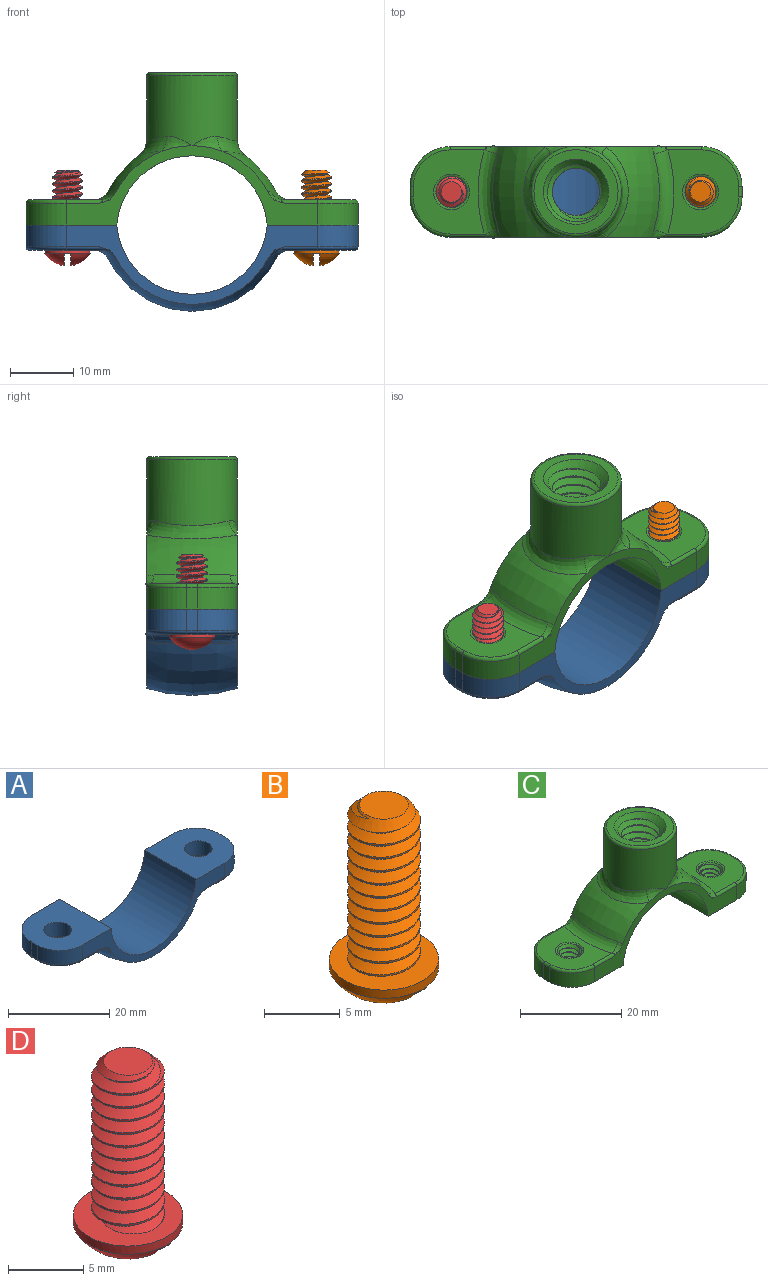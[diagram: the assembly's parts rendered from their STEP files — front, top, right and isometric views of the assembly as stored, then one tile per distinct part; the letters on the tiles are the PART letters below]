
ASSEMBLY  parts=4 mates=3
PART A: 34 faces, bbox 54.3x18.3x14.5 mm
  f0: revolved ~26.09x14.29mm, area 452.7mm2, adj f3,f4,f28,f29,f30,f31,f32,f33
  f1: plane 14.33x14.29mm, normal (0,0,1), area 164.3mm2, adj f3,f4,f5,f8,f10,f11,f14
  f2: plane 14.33x14.29mm, normal (0,0,1), area 164.3mm2, adj f3,f4,f5,f6,f12,f13,f15
  f3: plane 40.53x13.36mm, normal (0,-1,0), area 108.2mm2, adj f0,f1,f2,f5,f10,f13,f16,f21
  f4: plane 40.53x13.36mm, normal (0,1,0), area 108.2mm2, adj f0,f1,f2,f5,f11,f12,f20,f25
  f5: cylinder r=11.91mm len=23.73mm, axis (0,1,0), area 506.1mm2, adj f1,f2,f3,f4
  f6: plane 3.45x1.59mm, normal (-1,0,0), area 5.5mm2, adj f2,f12,f13,f18
  f7: plane 13.28x11.21mm, normal (0,0,-1), area 92.8mm2, adj f16,f17,f18,f19,f20,f26,f32
  f8: plane 3.45x1.59mm, normal (1,0,0), area 5.5mm2, adj f1,f10,f11,f23
  f9: plane 13.28x11.21mm, normal (0,0,-1), area 92.8mm2, adj f21,f22,f23,f24,f25,f27,f29
  f10: cylinder r=6.35mm len=6.35mm, axis (0,0,1), area 34.5mm2, adj f1,f3,f8,f22
  f11: cylinder r=6.35mm len=6.35mm, axis (0,0,-1), area 34.5mm2, adj f1,f4,f8,f24
  f12: cylinder r=6.35mm len=6.35mm, axis (0,0,1), area 34.5mm2, adj f2,f4,f6,f19
  f13: cylinder r=6.35mm len=6.35mm, axis (0,0,-1), area 34.5mm2, adj f2,f3,f6,f17
  f14: cylinder r=2.71mm len=5.43mm, axis (0,0,1), area 58.9mm2, adj f1,f27
  f15: cylinder r=2.71mm len=5.43mm, axis (0,0,1), area 58.9mm2, adj f2,f26
  f16: cylinder r=0.51mm len=5.69mm, axis (1,0,0), area 4.4mm2, adj f3,f7,f17,f31
  f17: torus R=5.84mm, axis (0,0,1), area 7.7mm2, adj f7,f13,f16,f18
  f18: cylinder r=0.51mm len=1.59mm, axis (0,1,0), area 1.3mm2, adj f6,f7,f17,f19
  f19: torus R=5.84mm, axis (0,0,1), area 7.7mm2, adj f7,f12,f18,f20
  f20: cylinder r=0.51mm len=5.69mm, axis (-1,0,0), area 4.4mm2, adj f4,f7,f19,f33
  f21: cylinder r=0.51mm len=5.69mm, axis (1,0,0), area 4.4mm2, adj f3,f9,f22,f30
  f22: torus R=5.84mm, axis (0,0,1), area 7.7mm2, adj f9,f10,f21,f23
  f23: cylinder r=0.51mm len=1.59mm, axis (0,1,0), area 1.3mm2, adj f8,f9,f22,f24
  f24: torus R=5.84mm, axis (0,0,1), area 7.7mm2, adj f9,f11,f23,f25
  f25: cylinder r=0.51mm len=5.69mm, axis (-1,0,0), area 4.4mm2, adj f4,f9,f24,f28
  f26: torus R=3.22mm, axis (0,0,1), area 14.5mm2, adj f7,f15
  f27: torus R=3.22mm, axis (0,0,1), area 14.5mm2, adj f9,f14
  f28: bspline ~3.28x3.16mm, area 3.5mm2, adj f0,f4,f25,f29
  f29: bspline ~17.42x3.8mm, area 36.1mm2, adj f0,f9,f28,f30
  f30: bspline ~3.28x3.16mm, area 3.5mm2, adj f0,f3,f21,f29
  f31: bspline ~3.28x3.16mm, area 3.5mm2, adj f0,f3,f16,f32
  f32: bspline ~17.42x3.8mm, area 36.1mm2, adj f0,f7,f31,f33
  f33: bspline ~3.28x3.16mm, area 3.5mm2, adj f0,f4,f20,f32
PART B: 13 faces, bbox 14.6x14.6x22.9 mm
  f0: sphere r=4.29mm, area 22.6mm2, adj f2,f10
  f1: sphere r=4.29mm, area 0mm2, adj f2,f11
  f2: cylinder r=3.62mm len=7.24mm, axis (0,0,1), area 15.1mm2, adj f0,f1,f3,f12
  f3: plane 7.65x7.65mm, normal (0,0,1), area 27.5mm2, adj f2,f4,f7,f8,f9
  f4: cylinder r=2.41mm len=11.65mm, axis (0,0,1), area -76.9mm2, adj f3,f6,f7,f8
  f5: plane 3.24x3.24mm, normal (0,0,1), area 8.2mm2, adj f6
  f6: cone r=1.62mm half-angle=45deg, axis (0,0,-1), area 7.6mm2, adj f4,f5,f7,f8,f9
  f7: bspline ~13.36x4.83mm, area 116.7mm2, adj f3,f4,f6,f9
  f8: bspline ~12.96x4.83mm, area 117.5mm2, adj f3,f4,f6,f9
  f9: bspline ~12.6x3.45mm, area 16.7mm2, adj f3,f6,f7,f8
  f10: plane 7.17x1.96mm, normal (1,0,0), area 9.9mm2, adj f0,f12
  f11: plane 14.58x9.36mm, normal (-1,0,0), area 9.9mm2, adj f1,f12
  f12: plane 7.24x0.97mm, normal (0,0,-1), area 7mm2, adj f2,f10,f11
PART C: 63 faces, bbox 54.8x18.8x26.1 mm
  f0: plane 14.33x14.29mm, normal (0,0,-1), area 166.1mm2, adj f4,f7,f8,f10,f11,f12,f37
  f1: plane 13.28x11.21mm, normal (0,0,1), area 100.5mm2, adj f43,f44,f45,f46,f47,f50,f52
  f2: plane 14.33x14.29mm, normal (0,0,-1), area 166.1mm2, adj f4,f7,f8,f9,f13,f14,f36
  f3: plane 13.28x11.21mm, normal (0,0,1), area 100.5mm2, adj f38,f39,f40,f41,f42,f49,f55
  f4: cylinder r=11.91mm len=23.73mm, axis (0,1,0), area 431.2mm2, adj f0,f2,f7,f8,f17,f18,f19,f20
  f5: revolved ~14.29x8.32mm, area 116.8mm2, adj f7,f8,f51,f52,f53,f58
  f6: revolved ~14.29x8.32mm, area 116.8mm2, adj f7,f8,f54,f55,f56,f61
  f7: plane 41.06x13.89mm, normal (0,-1,0), area 108.2mm2, adj f0,f2,f4,f5,f6,f11,f14,f38
  f8: plane 41.06x13.89mm, normal (0,1,0), area 108.2mm2, adj f0,f2,f4,f5,f6,f12,f13,f42
  f9: plane 3.45x1.59mm, normal (-1,0,0), area 5.5mm2, adj f2,f13,f14,f40
  f10: plane 3.45x1.59mm, normal (1,0,0), area 5.5mm2, adj f0,f11,f12,f45
  f11: cylinder r=6.35mm len=6.35mm, axis (0,0,-1), area 34.5mm2, adj f0,f7,f10,f44
  f12: cylinder r=6.35mm len=6.35mm, axis (0,0,1), area 34.5mm2, adj f0,f8,f10,f46
  f13: cylinder r=6.35mm len=6.35mm, axis (0,0,-1), area 34.5mm2, adj f2,f8,f9,f41
  f14: cylinder r=6.35mm len=6.35mm, axis (0,0,1), area 34.5mm2, adj f2,f7,f9,f39
  f15: cylinder r=7.14mm len=14.29mm, axis (0,0,1), area 444.6mm2, adj f48,f57,f58,f59,f60,f61,f62
  f16: plane 13.27x13.27mm, normal (0,0,1), area 55.2mm2, adj f24,f48
  f17: cylinder r=4.76mm len=13.38mm, axis (0,0,1), area 61mm2, adj f4,f18,f19,f20,f22,f24
  f18: bspline ~14.29x9.53mm, area 247.8mm2, adj f4,f17,f21,f23,f24
  f19: bspline ~13.44x9.52mm, area 245.9mm2, adj f4,f17,f21,f23,f24
  f20: bspline ~8.13x4.76mm, area 0.6mm2, adj f4,f17,f22
  f21: cone r=5.14mm half-angle=45deg, axis (0,0,-1), area 16mm2, adj f4,f18,f19,f23
  f22: cone r=5.14mm half-angle=45deg, axis (0,0,-1), area 4.6mm2, adj f4,f17,f20
  f23: bspline ~11.72x7.45mm, area 33.1mm2, adj f18,f19,f21,f24
  f24: cone r=5.14mm half-angle=45deg, axis (0,0,1), area 36.8mm2, adj f16,f17,f18,f19,f23
  f25: cylinder r=2.41mm len=4.83mm, axis (0,0,1), area 6.8mm2, adj f26,f27,f35,f36
  f26: bspline ~4.83x4.83mm, area 28.6mm2, adj f25,f28,f35,f36
  f27: bspline ~4.83x4.83mm, area 28.6mm2, adj f25,f28,f35,f36
  f28: bspline ~3.45x3.45mm, area 3mm2, adj f26,f27,f35,f36
  f29: cylinder r=2.41mm len=4.83mm, axis (0,0,1), area 6.8mm2, adj f30,f31,f33,f37
  f30: bspline ~4.83x4.83mm, area 28.6mm2, adj f29,f32,f34,f37
  f31: bspline ~4.83x4.83mm, area 28.6mm2, adj f29,f32,f33,f34,f37
  f32: bspline ~3.45x3.45mm, area 3mm2, adj f30,f31,f34,f37
  f33: cone r=2.61mm half-angle=45deg, axis (0,0,1), area 6mm2, adj f29,f31,f34,f50
  f34: cone r=2.61mm half-angle=45deg, axis (0,0,1), area 1.5mm2, adj f30,f31,f32,f33
  f35: cone r=2.61mm half-angle=45deg, axis (0,0,1), area 7.5mm2, adj f25,f26,f27,f28,f49
  f36: cone r=2.61mm half-angle=45deg, axis (0,0,-1), area 10.9mm2, adj f2,f25,f26,f27,f28
  f37: cone r=2.61mm half-angle=45deg, axis (0,0,-1), area 10.9mm2, adj f0,f29,f30,f31,f32
  f38: cylinder r=0.51mm len=5.69mm, axis (1,0,0), area 4.4mm2, adj f3,f7,f39,f54
  f39: torus R=5.84mm, axis (0,0,-1), area 7.7mm2, adj f3,f14,f38,f40
  f40: cylinder r=0.51mm len=1.59mm, axis (0,1,0), area 1.3mm2, adj f3,f9,f39,f41
  f41: torus R=5.84mm, axis (0,0,-1), area 7.7mm2, adj f3,f13,f40,f42
  f42: cylinder r=0.51mm len=5.69mm, axis (-1,0,0), area 4.4mm2, adj f3,f8,f41,f56
  f43: cylinder r=0.51mm len=5.69mm, axis (1,0,0), area 4.4mm2, adj f1,f7,f44,f53
  f44: torus R=5.84mm, axis (0,0,-1), area 7.7mm2, adj f1,f11,f43,f45
  f45: cylinder r=0.51mm len=1.59mm, axis (0,1,0), area 1.3mm2, adj f1,f10,f44,f46
  f46: torus R=5.84mm, axis (0,0,-1), area 7.7mm2, adj f1,f12,f45,f47
  f47: cylinder r=0.51mm len=5.69mm, axis (-1,0,0), area 4.4mm2, adj f1,f8,f46,f51
  f48: torus R=6.64mm, axis (0,0,1), area 34.9mm2, adj f15,f16
  f49: torus R=2.82mm, axis (0,0,-1), area 6.6mm2, adj f3,f35
  f50: torus R=2.82mm, axis (0,0,-1), area 6.6mm2, adj f1,f33
  f51: bspline ~3.28x3.16mm, area 3.5mm2, adj f5,f8,f47,f52
  f52: bspline ~17.42x3.8mm, area 36.1mm2, adj f1,f5,f51,f53
  f53: bspline ~3.28x3.16mm, area 3.5mm2, adj f5,f7,f43,f52
  f54: bspline ~3.28x3.16mm, area 3.5mm2, adj f6,f7,f38,f55
  f55: bspline ~17.42x3.8mm, area 36.1mm2, adj f3,f6,f54,f56
  f56: bspline ~3.28x3.16mm, area 3.5mm2, adj f6,f8,f42,f55
  f57: bspline ~5.44x2.6mm, area 4mm2, adj f8,f15,f58
  f58: bspline ~16.17x5.66mm, area 38.6mm2, adj f5,f15,f57,f59
  f59: bspline ~5.44x2.6mm, area 4mm2, adj f7,f15,f58
  f60: bspline ~5.44x2.6mm, area 4mm2, adj f7,f15,f61
  f61: bspline ~16.17x5.66mm, area 38.6mm2, adj f6,f15,f60,f62
  f62: bspline ~5.44x2.6mm, area 4mm2, adj f8,f15,f61
PART D: 13 faces, bbox 14.6x14.6x22.9 mm
  f0: sphere r=4.29mm, area 22.6mm2, adj f2,f10
  f1: sphere r=4.29mm, area 0mm2, adj f2,f11
  f2: cylinder r=3.62mm len=7.24mm, axis (0,0,1), area 15.1mm2, adj f0,f1,f3,f12
  f3: plane 7.65x7.65mm, normal (0,0,1), area 27.5mm2, adj f2,f4,f7,f8,f9
  f4: cylinder r=2.41mm len=11.65mm, axis (0,0,1), area -76.9mm2, adj f3,f6,f7,f8
  f5: plane 3.24x3.24mm, normal (0,0,1), area 8.2mm2, adj f6
  f6: cone r=1.62mm half-angle=45deg, axis (0,0,-1), area 7.6mm2, adj f4,f5,f7,f8,f9
  f7: bspline ~13.36x4.83mm, area 116.7mm2, adj f3,f4,f6,f9
  f8: bspline ~12.96x4.83mm, area 117.5mm2, adj f3,f4,f6,f9
  f9: bspline ~12.6x3.45mm, area 16.7mm2, adj f3,f6,f7,f8
  f10: plane 7.17x1.96mm, normal (-1,0,0), area 9.9mm2, adj f0,f12
  f11: plane 14.58x9.36mm, normal (1,0,0), area 9.9mm2, adj f1,f12
  f12: plane 7.24x0.97mm, normal (0,0,-1), area 7mm2, adj f2,f10,f11
PLACE A t=(-22.29,-9.63,-0.36)mm fixed
PLACE B t=(-22.29,-9.63,-0.21)mm
PLACE C t=(-22.29,-9.63,-2.34)mm
PLACE D t=(-22.29,-9.63,-0.21)mm
MATE fastened A.f15 <-> D.f2  axis (0,0,1) through (-41.93,-9.63,-1.35)mm
MATE fastened A.f14 <-> B.f2  axis (0,0,1) through (-2.64,-9.63,-1.35)mm
MATE fastened A.f2 <-> C.f2  axis (0,0,1) through (-34.15,-16.78,-1.35)mm
